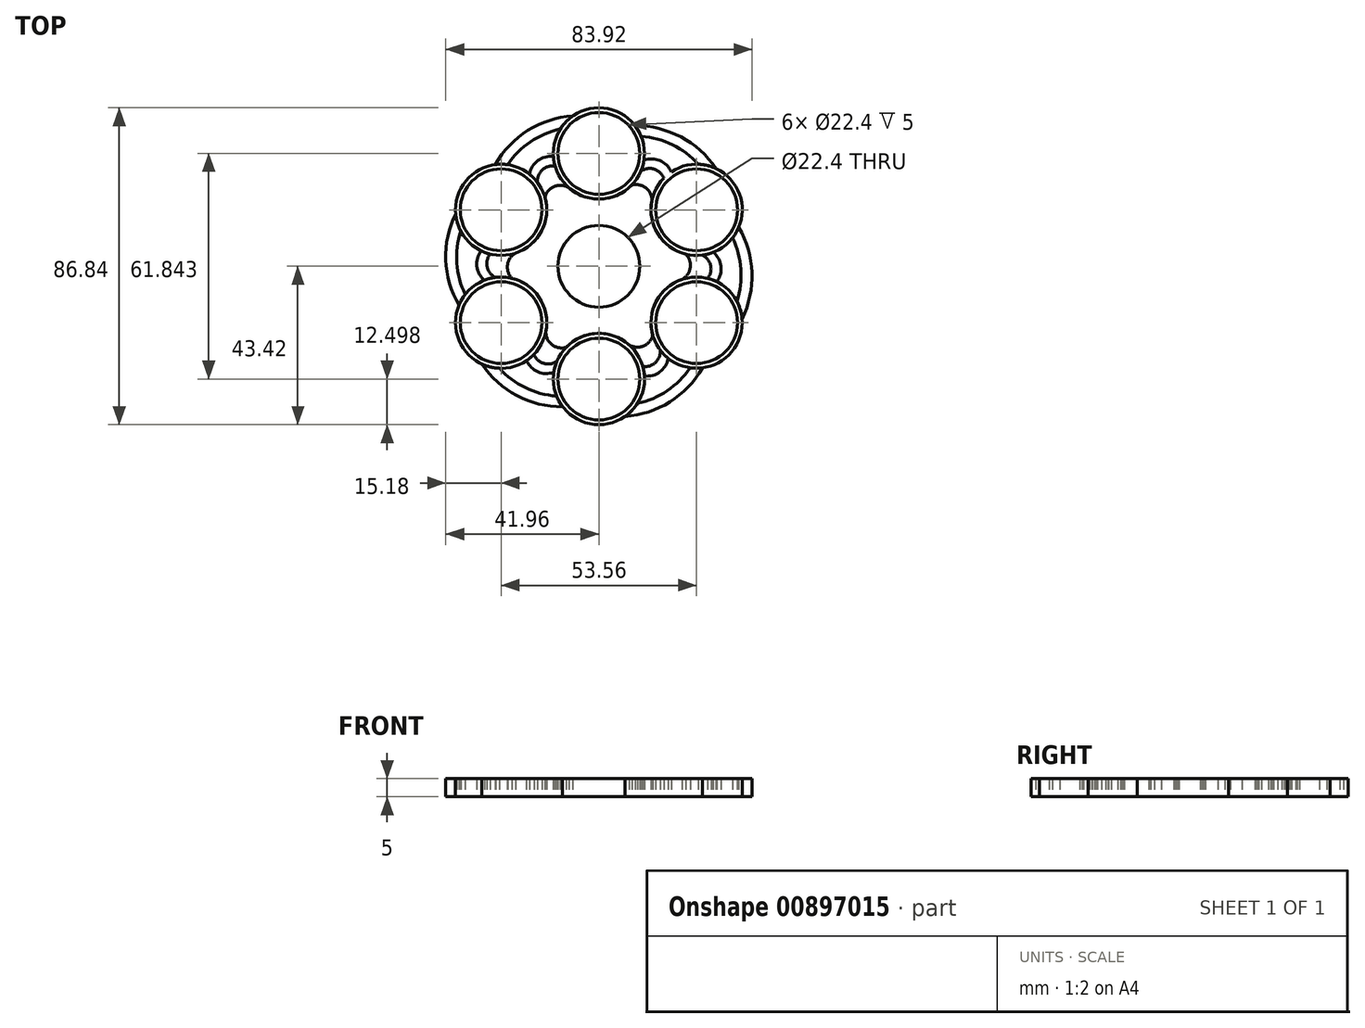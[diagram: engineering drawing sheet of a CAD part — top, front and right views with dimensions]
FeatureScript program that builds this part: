
annotation { "Feature Type Name" : "Feature", "Feature Type Description" : "" }
export const myFeature = defineFeature(function(context is Context, id is Id, definition is map)
    precondition{}
    {
        {
            var Q0;
            Q0=qCreatedBy(makeId("Top.planeOp"),FACE);
            var sketch = newSketch(context, id + "F0", { "sketchPlane" : qUnion([Q0])});
            skCircle(sketch, "E0", {"center": v(0, 0) * mm, "radius": 11.2 * mm});
            skCircle(sketch, "E1", {"center": v(0, 30.92) * mm, "radius": 12.5 * mm});
            skCircle(sketch, "E2.1.0", {"center": v(-26.78, 15.46) * mm, "radius": 12.5 * mm});
            skCircle(sketch, "E2.1.1", {"center": v(-26.78, 15.46) * mm, "radius": 11.2 * mm});
            skCircle(sketch, "E2.2.0", {"center": v(-26.78, -15.46) * mm, "radius": 12.5 * mm});
            skCircle(sketch, "E2.2.1", {"center": v(-26.78, -15.46) * mm, "radius": 11.2 * mm});
            skCircle(sketch, "E2.3.0", {"center": v(0, -30.92) * mm, "radius": 12.5 * mm});
            skCircle(sketch, "E2.3.1", {"center": v(0, -30.92) * mm, "radius": 11.2 * mm});
            skCircle(sketch, "E2.4.0", {"center": v(26.78, -15.46) * mm, "radius": 12.5 * mm});
            skCircle(sketch, "E2.4.1", {"center": v(26.78, -15.46) * mm, "radius": 11.2 * mm});
            skCircle(sketch, "E2.5.0", {"center": v(26.78, 15.46) * mm, "radius": 12.5 * mm});
            skCircle(sketch, "E2.5.1", {"center": v(26.78, 15.46) * mm, "radius": 11.2 * mm});
            skArc(sketch, "E3", {"start": v(-22.78, 3.61) * mm, "mid": v(-25.03, 0.4) * mm, "end": v(-23.78, -3.33) * mm});
            skArc(sketch, "E4.1.0", {"start": v(-14.52, -17.92) * mm, "mid": v(-12.85, -21.48) * mm, "end": v(-9, -22.25) * mm});
            skArc(sketch, "E4.2.0", {"start": v(8.26, -21.54) * mm, "mid": v(12.17, -21.87) * mm, "end": v(14.77, -18.93) * mm});
            skArc(sketch, "E4.3.0", {"start": v(22.78, -3.61) * mm, "mid": v(25.03, -0.4) * mm, "end": v(23.78, 3.33) * mm});
            skArc(sketch, "E4.4.0", {"start": v(14.52, 17.92) * mm, "mid": v(12.85, 21.48) * mm, "end": v(9, 22.25) * mm});
            skArc(sketch, "E4.5.0", {"start": v(-8.26, 21.54) * mm, "mid": v(-12.17, 21.87) * mm, "end": v(-14.77, 18.93) * mm});
            skArc(sketch, "E5", {"start": v(29.8, -3.33) * mm, "mid": v(30.61, 0.22) * mm, "end": v(28.32, 3.06) * mm});
            skArc(sketch, "E6", {"start": v(32.3, -4.24) * mm, "mid": v(33.43, -0.02) * mm, "end": v(31.35, 3.83) * mm});
            skArc(sketch, "E7", {"start": v(37.84, -9.63) * mm, "mid": v(38.92, -0.83) * mm, "end": v(36.6, 7.74) * mm});
            skArc(sketch, "E8", {"start": v(39.24, -14.4) * mm, "mid": v(41.94, -1.76) * mm, "end": v(38.32, 10.65) * mm});
            skArc(sketch, "E9.1.0", {"start": v(17.79, 24.14) * mm, "mid": v(15.11, 26.62) * mm, "end": v(11.51, 26.06) * mm});
            skArc(sketch, "E9.1.1", {"start": v(27.26, 27.95) * mm, "mid": v(20.18, 33.3) * mm, "end": v(11.6, 35.57) * mm});
            skArc(sketch, "E9.1.2", {"start": v(32.09, 26.78) * mm, "mid": v(22.5, 35.45) * mm, "end": v(9.93, 38.51) * mm});
            skArc(sketch, "E9.1.3", {"start": v(19.82, 25.85) * mm, "mid": v(16.73, 28.94) * mm, "end": v(12.36, 29.06) * mm});
            skArc(sketch, "E9.2.0", {"start": v(-12.02, 27.47) * mm, "mid": v(-15.5, 26.4) * mm, "end": v(-16.81, 23) * mm});
            skArc(sketch, "E9.2.1", {"start": v(-10.58, 37.59) * mm, "mid": v(-18.75, 34.12) * mm, "end": v(-25, 27.83) * mm});
            skArc(sketch, "E9.2.2", {"start": v(-7.15, 41.18) * mm, "mid": v(-19.45, 37.2) * mm, "end": v(-28.39, 27.86) * mm});
            skArc(sketch, "E9.2.3", {"start": v(-12.47, 30.09) * mm, "mid": v(-16.7, 28.96) * mm, "end": v(-19, 25.23) * mm});
            skArc(sketch, "E9.3.0", {"start": v(-29.8, 3.33) * mm, "mid": v(-30.61, -0.22) * mm, "end": v(-28.32, -3.06) * mm});
            skArc(sketch, "E9.3.1", {"start": v(-37.84, 9.63) * mm, "mid": v(-38.92, 0.83) * mm, "end": v(-36.6, -7.74) * mm});
            skArc(sketch, "E9.3.2", {"start": v(-39.24, 14.4) * mm, "mid": v(-41.94, 1.76) * mm, "end": v(-38.32, -10.65) * mm});
            skArc(sketch, "E9.3.3", {"start": v(-32.3, 4.24) * mm, "mid": v(-33.43, 0.02) * mm, "end": v(-31.35, -3.83) * mm});
            skArc(sketch, "E9.4.0", {"start": v(-17.79, -24.14) * mm, "mid": v(-15.11, -26.62) * mm, "end": v(-11.51, -26.06) * mm});
            skArc(sketch, "E9.4.1", {"start": v(-27.26, -27.95) * mm, "mid": v(-20.18, -33.3) * mm, "end": v(-11.6, -35.57) * mm});
            skArc(sketch, "E9.4.2", {"start": v(-32.09, -26.78) * mm, "mid": v(-22.5, -35.45) * mm, "end": v(-9.93, -38.51) * mm});
            skArc(sketch, "E9.4.3", {"start": v(-19.82, -25.85) * mm, "mid": v(-16.73, -28.94) * mm, "end": v(-12.36, -29.06) * mm});
            skArc(sketch, "E9.5.0", {"start": v(12.02, -27.47) * mm, "mid": v(15.5, -26.4) * mm, "end": v(16.81, -23) * mm});
            skArc(sketch, "E9.5.1", {"start": v(10.58, -37.59) * mm, "mid": v(18.75, -34.12) * mm, "end": v(25, -27.83) * mm});
            skArc(sketch, "E9.5.2", {"start": v(7.15, -41.18) * mm, "mid": v(19.45, -37.2) * mm, "end": v(28.39, -27.86) * mm});
            skArc(sketch, "E9.5.3", {"start": v(12.47, -30.09) * mm, "mid": v(16.7, -28.96) * mm, "end": v(19, -25.23) * mm});
            skCircle(sketch, "E10", {"center": v(0, 30.92) * mm, "radius": 11.2 * mm});
            skPoint(sketch, "E11.orphan", {"position": v(-6.33, -20.14) * mm});
            skPoint(sketch, "E12.orphan", {"position": v(-20.61, -4.6) * mm});
            skPoint(sketch, "E13.orphan", {"position": v(-14.28, 15.55) * mm});
            skPoint(sketch, "E14.orphan", {"position": v(6.33, 20.14) * mm});
            skPoint(sketch, "E15.orphan", {"position": v(20.61, 4.6) * mm});
            skPoint(sketch, "E16.orphan", {"position": v(14.28, -15.55) * mm});
            skSolve(sketch);
        }
        {
            var Q0;
            Q0=makeQuery(id+"F0.imprint","IMPRINT",FACE,{"disambiguationData":[TD([[makeQuery(id+"F0.imprint","IMPRINT",EDGE,{"derivedFrom":sQuery(id+"F0.wireOp",EDGE,"E0")}),-1.0]])]});
            var Q1;
            {var subQ0=sQuery(id+"F0.wireOp",EDGE,"E9.2.0");Q1=makeQuery(id+"F0.imprint","IMPRINT",FACE,{"disambiguationData":[TD([[makeQuery(id+"F0.imprint","IMPRINT",EDGE,{"derivedFrom":subQ0}),-1.0]])]});}
            var Q2;
            {var subQ0=sQuery(id+"F0.wireOp",EDGE,"E9.2.1");Q2=makeQuery(id+"F0.imprint","IMPRINT",FACE,{"disambiguationData":[TD([[makeQuery(id+"F0.imprint","IMPRINT",EDGE,{"derivedFrom":subQ0}),-1.0]])]});}
            var Q3;
            {var subQ0=sQuery(id+"F0.wireOp",EDGE,"E9.1.1");Q3=makeQuery(id+"F0.imprint","IMPRINT",FACE,{"disambiguationData":[TD([[makeQuery(id+"F0.imprint","IMPRINT",EDGE,{"derivedFrom":subQ0}),-1.0]])]});}
            var Q4;
            {var subQ0=sQuery(id+"F0.wireOp",EDGE,"E7");Q4=makeQuery(id+"F0.imprint","IMPRINT",FACE,{"disambiguationData":[TD([[makeQuery(id+"F0.imprint","IMPRINT",EDGE,{"derivedFrom":subQ0}),-1.0]])]});}
            var Q5;
            {var subQ0=sQuery(id+"F0.wireOp",EDGE,"E5");Q5=makeQuery(id+"F0.imprint","IMPRINT",FACE,{"disambiguationData":[TD([[makeQuery(id+"F0.imprint","IMPRINT",EDGE,{"derivedFrom":subQ0}),-1.0]])]});}
            var Q6;
            {var subQ0=sQuery(id+"F0.wireOp",EDGE,"E9.5.1");Q6=makeQuery(id+"F0.imprint","IMPRINT",FACE,{"disambiguationData":[TD([[makeQuery(id+"F0.imprint","IMPRINT",EDGE,{"derivedFrom":subQ0}),-1.0]])]});}
            var Q7;
            {var subQ0=sQuery(id+"F0.wireOp",EDGE,"E9.5.0");Q7=makeQuery(id+"F0.imprint","IMPRINT",FACE,{"disambiguationData":[TD([[makeQuery(id+"F0.imprint","IMPRINT",EDGE,{"derivedFrom":subQ0}),-1.0]])]});}
            var Q8;
            {var subQ0=sQuery(id+"F0.wireOp",EDGE,"E9.4.1");Q8=makeQuery(id+"F0.imprint","IMPRINT",FACE,{"disambiguationData":[TD([[makeQuery(id+"F0.imprint","IMPRINT",EDGE,{"derivedFrom":subQ0}),-1.0]])]});}
            var Q9;
            {var subQ0=sQuery(id+"F0.wireOp",EDGE,"E9.4.0");Q9=makeQuery(id+"F0.imprint","IMPRINT",FACE,{"disambiguationData":[TD([[makeQuery(id+"F0.imprint","IMPRINT",EDGE,{"derivedFrom":subQ0}),-1.0]])]});}
            var Q10;
            {var subQ0=sQuery(id+"F0.wireOp",EDGE,"E9.3.1");Q10=makeQuery(id+"F0.imprint","IMPRINT",FACE,{"disambiguationData":[TD([[makeQuery(id+"F0.imprint","IMPRINT",EDGE,{"derivedFrom":subQ0}),-1.0]])]});}
            var Q11;
            {var subQ0=sQuery(id+"F0.wireOp",EDGE,"E9.3.0");Q11=makeQuery(id+"F0.imprint","IMPRINT",FACE,{"disambiguationData":[TD([[makeQuery(id+"F0.imprint","IMPRINT",EDGE,{"derivedFrom":subQ0}),-1.0]])]});}
            extrude(context, id + "F1", {"entities" : qUnion([Q0, Q1, Q2, Q3, Q4, Q5, Q6, Q7, Q8, Q9, Q10, Q11]), "depth" : 5 * mm, "offsetDistance" : 25 * mm});
        }
        {
            var Q0;
            Q0=makeQuery(id+"F0.imprint","IMPRINT",FACE,{"disambiguationData":[TD([[makeQuery(id+"F0.imprint","IMPRINT",EDGE,{"derivedFrom":sQuery(id+"F0.wireOp",EDGE,"E2.1.1")}),-1.0]])]});
            var Q1;
            Q1=makeQuery(id+"F0.imprint","IMPRINT",FACE,{"disambiguationData":[TD([[makeQuery(id+"F0.imprint","IMPRINT",EDGE,{"derivedFrom":sQuery(id+"F0.wireOp",EDGE,"41d47bc2-2364-45cc-956a-842994b4d414")}),-1.0]])]});
            var Q2;
            Q2=makeQuery(id+"F0.imprint","IMPRINT",FACE,{"disambiguationData":[TD([[makeQuery(id+"F0.imprint","IMPRINT",EDGE,{"derivedFrom":sQuery(id+"F0.wireOp",EDGE,"E2.5.1")}),-1.0]])]});
            var Q3;
            Q3=makeQuery(id+"F0.imprint","IMPRINT",FACE,{"disambiguationData":[TD([[makeQuery(id+"F0.imprint","IMPRINT",EDGE,{"derivedFrom":sQuery(id+"F0.wireOp",EDGE,"E2.4.1")}),-1.0]])]});
            var Q4;
            Q4=makeQuery(id+"F0.imprint","IMPRINT",FACE,{"disambiguationData":[TD([[makeQuery(id+"F0.imprint","IMPRINT",EDGE,{"derivedFrom":sQuery(id+"F0.wireOp",EDGE,"E2.3.1")}),-1.0]])]});
            var Q5;
            Q5=makeQuery(id+"F0.imprint","IMPRINT",FACE,{"disambiguationData":[TD([[makeQuery(id+"F0.imprint","IMPRINT",EDGE,{"derivedFrom":sQuery(id+"F0.wireOp",EDGE,"E2.2.1")}),-1.0]])]});
            var Q6;
            {var subQ0=sQuery(id+"F0.wireOp",EDGE,"E9.1.0");Q6=makeQuery(id+"F0.imprint","IMPRINT",FACE,{"disambiguationData":[TD([[makeQuery(id+"F0.imprint","IMPRINT",EDGE,{"derivedFrom":subQ0}),-1.0]])]});}
            extrude(context, id + "F2", {"entities" : qUnion([Q0, Q1, Q2, Q3, Q4, Q5, Q6]), "depth" : 5 * mm, "offsetDistance" : 25 * mm});
        }
        {
            var Q0;
            Q0=makeQuery(id+"F0.imprint","IMPRINT",FACE,{"disambiguationData":[TD([[makeQuery(id+"F0.imprint","IMPRINT",EDGE,{"derivedFrom":sQuery(id+"F0.wireOp",EDGE,"E10")}),-1.0]])]});
            extrude(context, id + "F3", {"entities" : qUnion([Q0]), "depth" : 5 * mm, "offsetDistance" : 25 * mm});
        }
    });
